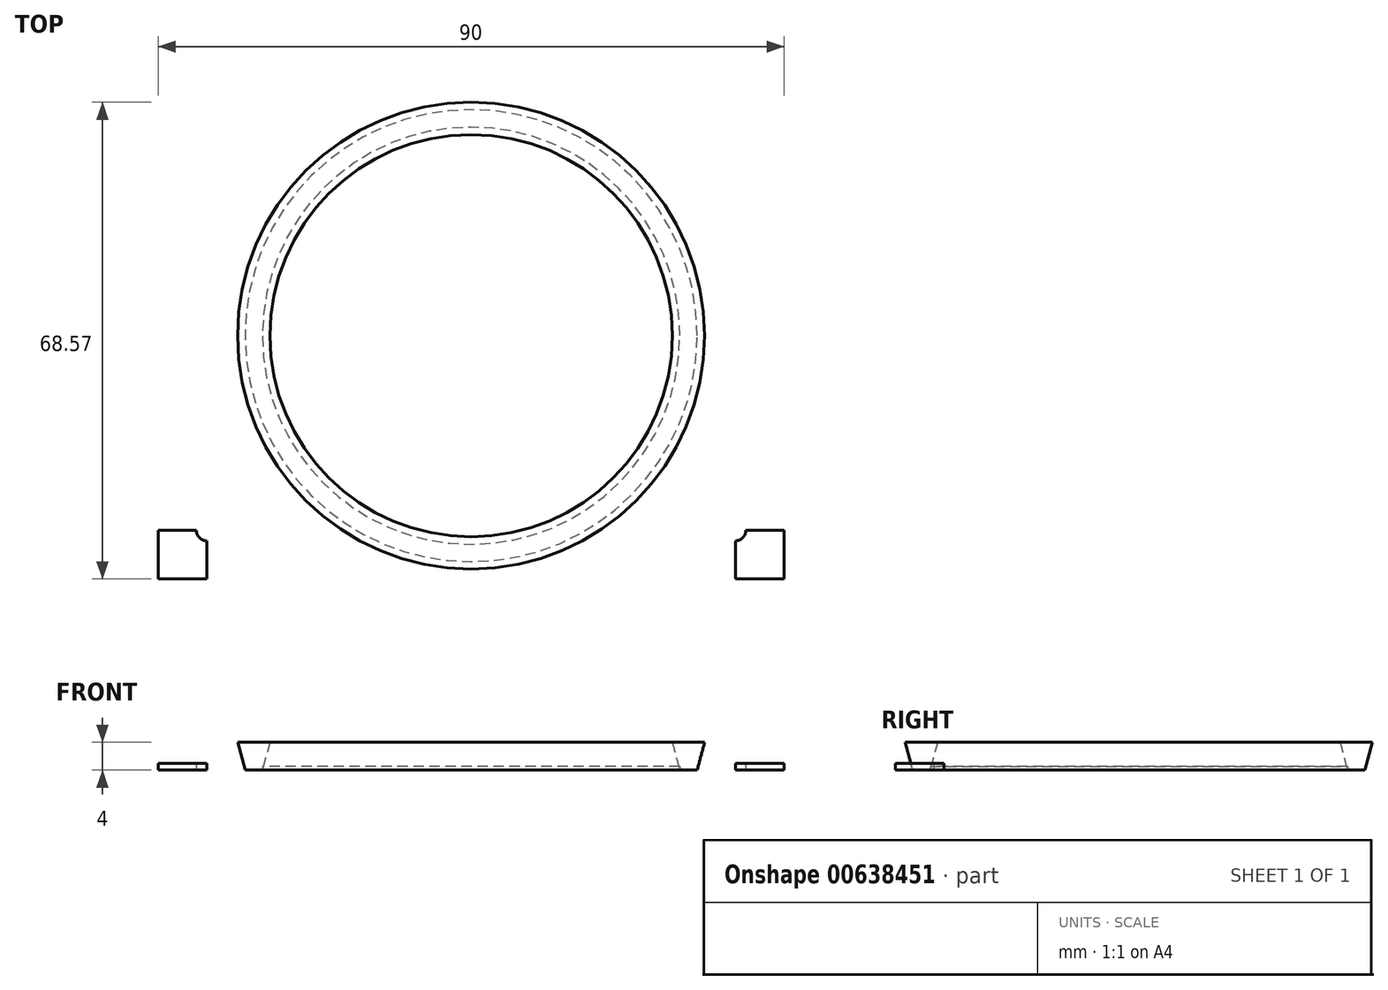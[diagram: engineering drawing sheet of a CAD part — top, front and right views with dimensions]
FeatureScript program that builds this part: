
annotation { "Feature Type Name" : "Feature", "Feature Type Description" : "" }
export const myFeature = defineFeature(function(context is Context, id is Id, definition is map)
    precondition{}
    {
        {
            var Q0;
            Q0=qCreatedBy(makeId("Top.planeOp"),FACE);
            var sketch = newSketch(context, id + "F0", { "sketchPlane" : qUnion([Q0])});
            skLineSegment(sketch, "E0.bottom", {"start": v(45, -35) * mm, "end": v(-45, -35) * mm});
            skLineSegment(sketch, "E0.top", {"start": v(45, 35) * mm, "end": v(-45, 35) * mm});
            skLineSegment(sketch, "E0.left", {"start": v(45, -35) * mm, "end": v(45, 35) * mm});
            skLineSegment(sketch, "E0.right", {"start": v(-45, -35) * mm, "end": v(-45, 35) * mm});
            skPoint(sketch, "E0.middle", {"position": v(0, 0) * mm});
            skCircle(sketch, "E1", {"center": v(0, 0) * mm, "radius": 32.5 * mm});
            skCircle(sketch, "E2", {"center": v(0, 0) * mm, "radius": 30 * mm});
            skLineSegment(sketch, "E3.bottom", {"start": v(-45, 35) * mm, "end": v(-38, 35) * mm});
            skLineSegment(sketch, "E3.top", {"start": v(-45, 28) * mm, "end": v(-38, 28) * mm});
            skLineSegment(sketch, "E3.left", {"start": v(-45, 35) * mm, "end": v(-45, 28) * mm});
            skLineSegment(sketch, "E3.right", {"start": v(-38, 35) * mm, "end": v(-38, 28) * mm});
            skLineSegment(sketch, "E4.bottom", {"start": v(-45, -35) * mm, "end": v(-38, -35) * mm});
            skLineSegment(sketch, "E4.top", {"start": v(-45, -28) * mm, "end": v(-38, -28) * mm});
            skLineSegment(sketch, "E4.left", {"start": v(-45, -35) * mm, "end": v(-45, -28) * mm});
            skLineSegment(sketch, "E4.right", {"start": v(-38, -35) * mm, "end": v(-38, -28) * mm});
            skLineSegment(sketch, "E5.bottom", {"start": v(45, -35) * mm, "end": v(38, -35) * mm});
            skLineSegment(sketch, "E5.top", {"start": v(45, -28) * mm, "end": v(38, -28) * mm});
            skLineSegment(sketch, "E5.left", {"start": v(45, -35) * mm, "end": v(45, -28) * mm});
            skLineSegment(sketch, "E5.right", {"start": v(38, -35) * mm, "end": v(38, -28) * mm});
            skLineSegment(sketch, "E6.bottom", {"start": v(45, 35) * mm, "end": v(38, 35) * mm});
            skLineSegment(sketch, "E6.top", {"start": v(45, 28) * mm, "end": v(38, 28) * mm});
            skLineSegment(sketch, "E6.left", {"start": v(45, 35) * mm, "end": v(45, 28) * mm});
            skLineSegment(sketch, "E6.right", {"start": v(38, 35) * mm, "end": v(38, 28) * mm});
            skCircle(sketch, "E7", {"center": v(-38, 28) * mm, "radius": 1.5 * mm});
            skCircle(sketch, "E8", {"center": v(-38, -28) * mm, "radius": 1.5 * mm});
            skCircle(sketch, "E9", {"center": v(38, -28) * mm, "radius": 1.5 * mm});
            skCircle(sketch, "E10", {"center": v(38, 28) * mm, "radius": 1.5 * mm});
            skSolve(sketch);
        }
        {
            var Q0;
            {var subQ5=sQuery(id+"F0.wireOp",EDGE,"E0.bottom");Q0=makeQuery(id+"F0.imprint","IMPRINT",FACE,{"disambiguationData":[TD([[makeQuery(id+"F0.imprint","IMPRINT",EDGE,{"derivedFrom":subQ5}),-1.0]])]});}
            var Q1;
            {var subQ1=sQuery(id+"F0.wireOp",EDGE,"E3.bottom");Q1=makeQuery(id+"F0.imprint","IMPRINT",FACE,{"disambiguationData":[TD([[makeQuery(id+"F0.imprint","IMPRINT",EDGE,{"derivedFrom":subQ1}),-1.0]])]});}
            var Q2;
            {var subQ1=sQuery(id+"F0.wireOp",EDGE,"E6.bottom");Q2=makeQuery(id+"F0.imprint","IMPRINT",FACE,{"disambiguationData":[TD([[makeQuery(id+"F0.imprint","IMPRINT",EDGE,{"derivedFrom":subQ1}),1.0]])]});}
            var Q3;
            {var subQ1=sQuery(id+"F0.wireOp",EDGE,"E5.bottom");Q3=makeQuery(id+"F0.imprint","IMPRINT",FACE,{"disambiguationData":[TD([[makeQuery(id+"F0.imprint","IMPRINT",EDGE,{"derivedFrom":subQ1}),-1.0]])]});}
            var Q4;
            {var subQ1=sQuery(id+"F0.wireOp",EDGE,"E4.bottom");Q4=makeQuery(id+"F0.imprint","IMPRINT",FACE,{"disambiguationData":[TD([[makeQuery(id+"F0.imprint","IMPRINT",EDGE,{"derivedFrom":subQ1}),1.0]])]});}
            extrude(context, id + "F1", {"entities" : qUnion([Q0, Q1, Q2, Q3, Q4]), "depth" : 1 * mm, "offsetDistance" : 25 * mm});
        }
        {
            var Q0;
            Q0=makeQuery(id+"F0.imprint","IMPRINT",FACE,{"disambiguationData":[TD([[makeQuery(id+"F0.imprint","IMPRINT",EDGE,{"derivedFrom":sQuery(id+"F0.wireOp",EDGE,"E2")}),1.0]])]});
            extrude(context, id + "F2", {"entities" : qUnion([Q0]), "depth" : 0.5 * mm, "offsetDistance" : 25 * mm});
        }
        {
            var Q0;
            Q0=makeQuery(id+"F0.imprint","IMPRINT",FACE,{"disambiguationData":[TD([[makeQuery(id+"F0.imprint","IMPRINT",EDGE,{"derivedFrom":sQuery(id+"F0.wireOp",EDGE,"E1")}),1.0]])]});
            extrude(context, id + "F3", {"entities" : qUnion([Q0]), "depth" : 4 * mm, "offsetDistance" : 25 * mm, "hasDraft" : true, "draftAngle" : 15 * degree});
        }
    });
